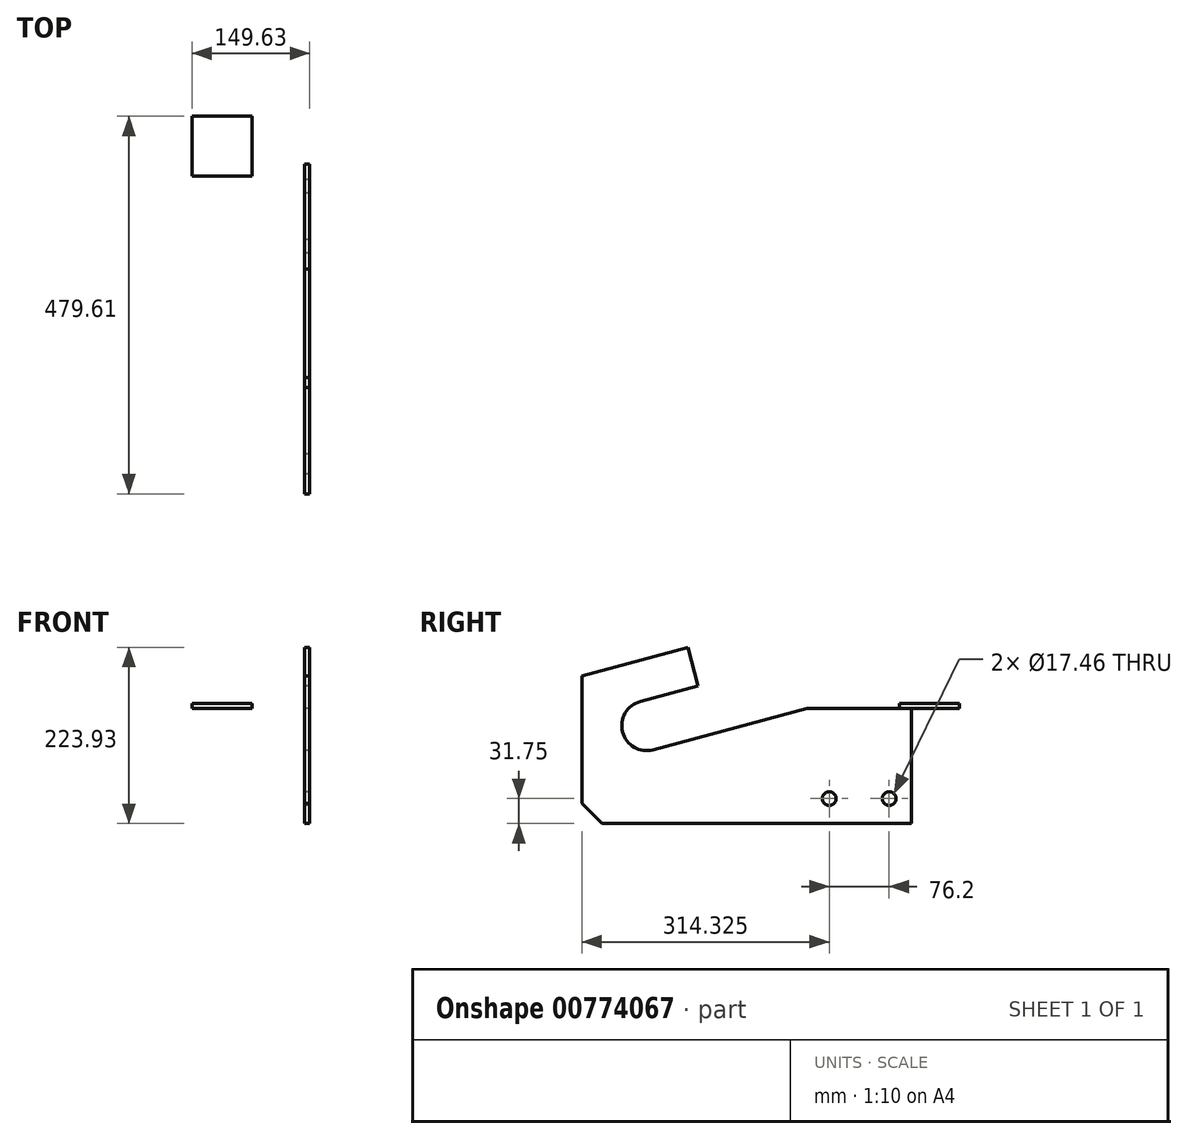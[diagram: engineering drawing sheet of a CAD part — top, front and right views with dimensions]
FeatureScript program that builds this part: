
annotation { "Feature Type Name" : "Feature", "Feature Type Description" : "" }
export const myFeature = defineFeature(function(context is Context, id is Id, definition is map)
    precondition{}
    {
        {
            var Q0;
            Q0=qCreatedBy(makeId("Right.planeOp"),FACE);
            var sketch = newSketch(context, id + "F0", { "sketchPlane" : qUnion([Q0])});
            skLineSegment(sketch, "E0", {"start": v(0, 0) * mm, "end": v(-194.98, -52.25) * mm});
            skArc(sketch, "E1", {"start": v(-211.42, 9.1) * mm, "mid": v(-233.87, -29.8) * mm, "end": v(-194.98, -52.25) * mm});
            skLineSegment(sketch, "E2", {"start": v(-211.42, 9.1) * mm, "end": v(-137.81, 28.81) * mm});
            skLineSegment(sketch, "E3", {"start": v(-137.81, 28.81) * mm, "end": v(-150.96, 77.88) * mm});
            skLineSegment(sketch, "E4", {"start": v(-150.96, 77.88) * mm, "end": v(-285.75, 41.77) * mm});
            skLineSegment(sketch, "E5", {"start": v(-285.75, 41.77) * mm, "end": v(-285.75, -120.65) * mm});
            skLineSegment(sketch, "E6", {"start": v(-203.2, -21.58) * mm, "end": v(0, 32.87) * mm, "construction": true});
            skLineSegment(sketch, "E7", {"start": v(0, 32.87) * mm, "end": v(-35.03, 32.87) * mm, "construction": true});
            skPoint(sketch, "E8", {"position": v(-234.95, -21.58) * mm});
            skLineSegment(sketch, "E9", {"start": v(0, -146.05) * mm, "end": v(-304.17, -146.05) * mm, "construction": true});
            skLineSegment(sketch, "E10", {"start": v(0, -146.05) * mm, "end": v(-260.35, -146.05) * mm});
            skLineSegment(sketch, "E11", {"start": v(-260.35, -146.05) * mm, "end": v(-285.75, -120.65) * mm});
            skLineSegment(sketch, "E12", {"start": v(0, 0) * mm, "end": v(133.35, 0) * mm});
            skLineSegment(sketch, "E13", {"start": v(133.35, 0) * mm, "end": v(133.35, -146.05) * mm});
            skLineSegment(sketch, "E14", {"start": v(133.35, -146.05) * mm, "end": v(0, -146.05) * mm});
            skLineSegment(sketch, "E15", {"start": v(28.58, 0) * mm, "end": v(28.58, -146.05) * mm, "construction": true});
            skCircle(sketch, "E16", {"center": v(104.78, -114.3) * mm, "radius": 8.73 * mm});
            skCircle(sketch, "E17", {"center": v(28.58, -114.3) * mm, "radius": 8.73 * mm});
            skLineSegment(sketch, "E18", {"start": v(0, 0) * mm, "end": v(133.35, 0) * mm, "construction": true});
            skPoint(sketch, "E19", {"position": v(28.58, -123.03) * mm});
            skPoint(sketch, "E20", {"position": v(-203.2, -53.33) * mm});
            skPoint(sketch, "E21", {"position": v(-203.2, -146.05) * mm});
            skSolve(sketch);
        }
        {
            var Q0;
            Q0=makeQuery(id+"F0.imprint","IMPRINT",FACE,{"disambiguationData":[TD([[makeQuery(id+"F0.imprint","IMPRINT",EDGE,{"derivedFrom":sQuery(id+"F0.wireOp",EDGE,"E0")}),1.0]])]});
            extrude(context, id + "F1", {"entities" : qUnion([Q0]), "depth" : 6.35 * mm, "offsetDistance" : 25.4 * mm});
        }
        {
            var Q0;
            Q0=qCreatedBy(makeId("Top.planeOp"),FACE);
            var sketch = newSketch(context, id + "F2", { "sketchPlane" : qUnion([Q0])});
            skLineSegment(sketch, "E22.bottom", {"start": v(-143.28, 193.86) * mm, "end": v(-67.08, 193.86) * mm});
            skLineSegment(sketch, "E22.top", {"start": v(-143.28, 117.66) * mm, "end": v(-67.08, 117.66) * mm});
            skLineSegment(sketch, "E22.left", {"start": v(-143.28, 193.86) * mm, "end": v(-143.28, 117.66) * mm});
            skLineSegment(sketch, "E22.right", {"start": v(-67.08, 193.86) * mm, "end": v(-67.08, 117.66) * mm});
            skSolve(sketch);
        }
        {
            var Q0;
            Q0=makeQuery(id+"F2.imprint","IMPRINT",FACE,{"disambiguationData":[TD([[makeQuery(id+"F2.imprint","IMPRINT",EDGE,{"derivedFrom":sQuery(id+"F2.wireOp",EDGE,"E22.bottom")}),-1.0]])]});
            extrude(context, id + "F3", {"entities" : qUnion([Q0]), "depth" : 6.35 * mm, "offsetDistance" : 25.4 * mm});
        }
    });
